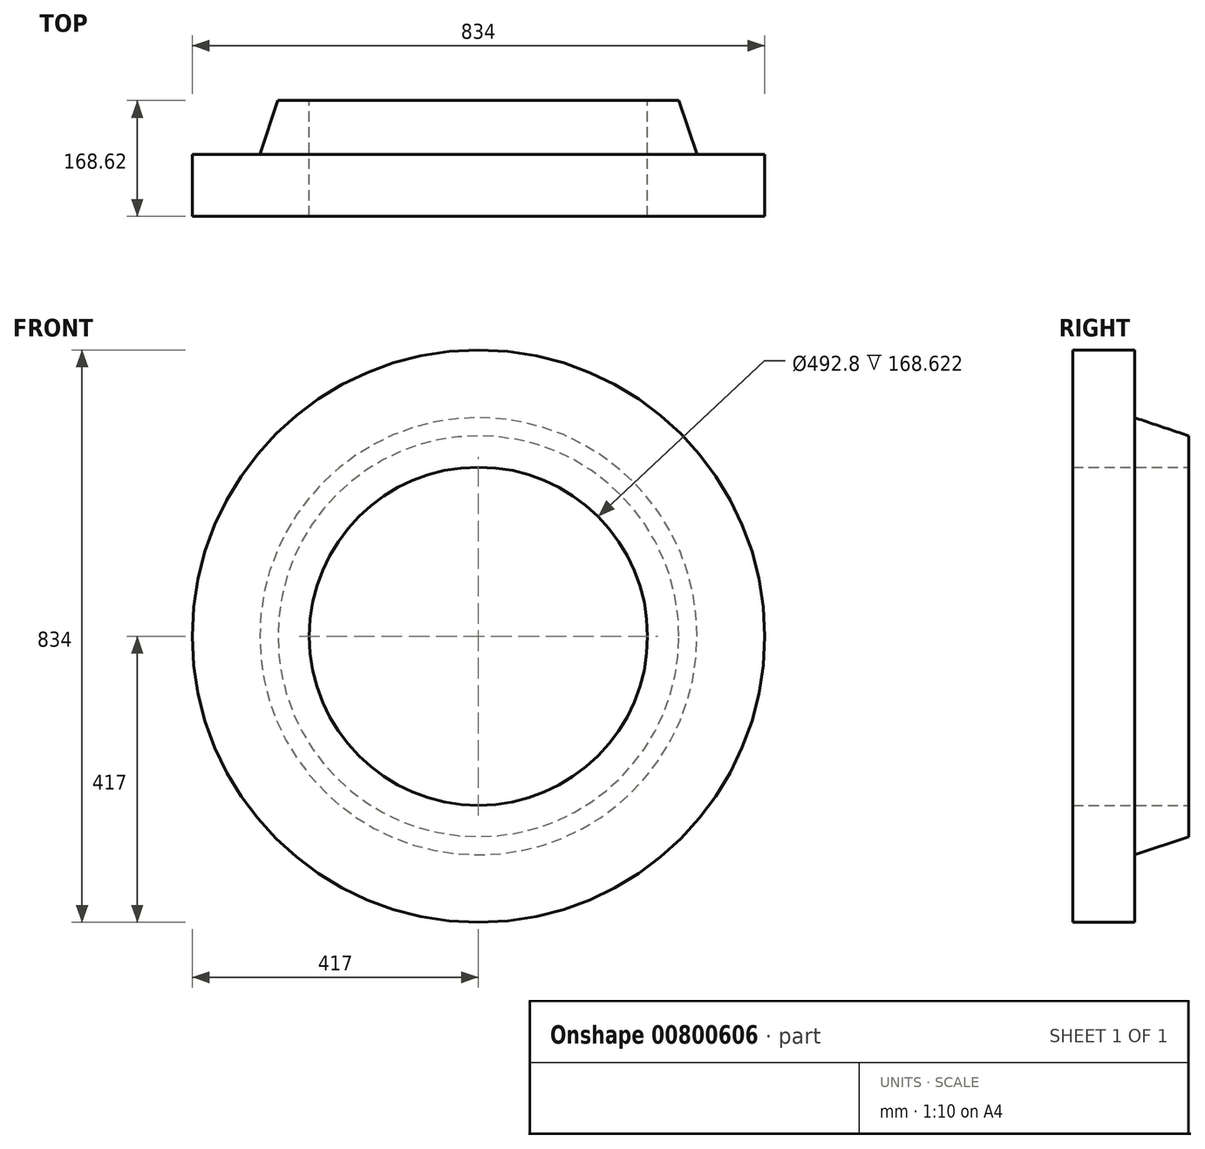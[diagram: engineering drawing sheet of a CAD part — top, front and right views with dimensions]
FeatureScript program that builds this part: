
annotation { "Feature Type Name" : "Feature", "Feature Type Description" : "" }
export const myFeature = defineFeature(function(context is Context, id is Id, definition is map)
    precondition{}
    {
        {
            var Q0;
            Q0=qCreatedBy(makeId("Right.planeOp"),FACE);
            var sketch = newSketch(context, id + "F0", { "sketchPlane" : qUnion([Q0])});
            skLineSegment(sketch, "E0", {"start": v(0, 246.4) * mm, "end": v(-168.62, 246.4) * mm});
            skLineSegment(sketch, "E1", {"start": v(-168.62, 246.4) * mm, "end": v(-168.62, 417) * mm});
            skLineSegment(sketch, "E2", {"start": v(-168.62, 417) * mm, "end": v(-78.78, 417) * mm});
            skLineSegment(sketch, "E3", {"start": v(-78.78, 417) * mm, "end": v(-78.78, 318.55) * mm});
            skLineSegment(sketch, "E4", {"start": v(-78.78, 318.55) * mm, "end": v(0, 292.1) * mm});
            skLineSegment(sketch, "E5", {"start": v(0, 292.1) * mm, "end": v(0, 246.4) * mm});
            skLineSegment(sketch, "E6", {"start": v(0, 0) * mm, "end": v(-298.74, 0) * mm, "construction": true});
            skSolve(sketch);
        }
        {
            var Q0;
            Q0=makeQuery(id+"F0.imprint","IMPRINT",FACE,{"disambiguationData":[TD([[makeQuery(id+"F0.imprint","IMPRINT",EDGE,{"derivedFrom":sQuery(id+"F0.wireOp",EDGE,"E0")}),-1.0]])]});
            var Q1;
            Q1=sQuery(id+"F0.wireOp",EDGE,"E6");
            revolve(context, id + "F1", {"surfaceOperationType" : NewSurfaceOperationType.NEW, "entities" : qUnion([Q0]), "axis" : qUnion([Q1]), "revolveType" : RevolveType.FULL});
        }
    });
